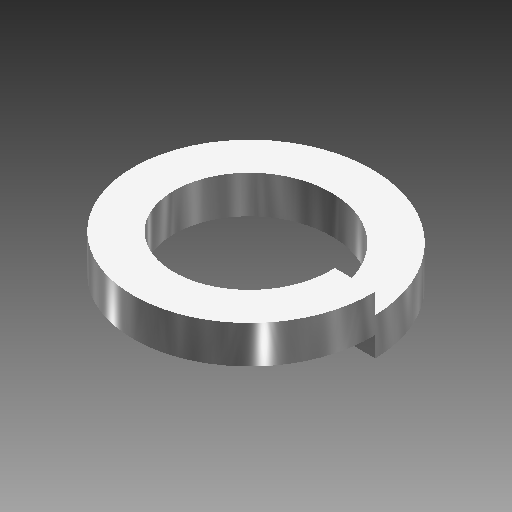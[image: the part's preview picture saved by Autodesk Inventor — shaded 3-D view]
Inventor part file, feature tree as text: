
AUTODESK INVENTOR PART (.ipt)
format: ipt  version: 2019 (Build 230136000, 136)  size: 126,464 bytes
history: native  units: in
note: dims shown in document units (in); Inventor stores cm internally (conversion verified against a paired STEP export)
features: helix x1, sketch x1
ambient origin geometry x8: Origin, YZ Plane, XZ Plane, XY Plane, X Axis, Y Axis, Z Axis, Center Point
bodies: Solid1 (feature_tree)
feature tree (2):
  helix  "Coil1"  [1 undecoded]
  sketch  "Sketch1"  dims[d1=0.037in d2=0.04in d3=0.02in d4=1.0in d5=0.3937in d6=0.0in d7=90.0deg d8=90.0deg d9=0.0in d10=0.0in]
note: 1 required parameter value undecoded (feature->parameter linkage not recoverable at this tier; creation-order binding heuristic only, values carry confidence <= 0.55)
